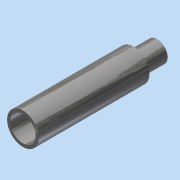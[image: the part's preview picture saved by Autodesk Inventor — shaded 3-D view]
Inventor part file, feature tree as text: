
AUTODESK INVENTOR PART (.ipt)
format: ipt  version: 2015 (Build 190159000, 159)  size: 100,352 bytes
history: native  units: in
note: dims shown in document units (in); Inventor stores cm internally (conversion verified against a paired STEP export)
features: extrude x3, sketch x3
ambient origin geometry x8: Origin, YZ Plane, XZ Plane, XY Plane, X Axis, Y Axis, Z Axis, Center Point
bodies: Solid1 (feature_tree)
feature tree (6):
  extrude  "Extrusion1"  Depth=0.5906in
  extrude  "Extrusion2"  Depth=2.0655in
  extrude  "Extrusion3"  Depth=0.4375in TaperAngle=0.0deg
  sketch  "Sketch1"  dims[d0=0.4724in d1=0.5906in]
  sketch  "Sketch2"  dims[d2=2.0655in d3=0.0in d4=0.3228in]
  sketch  "Sketch3"  dims[d5=0.3937in d6=0.4375in d7=0.0in d8=0.125in d9=0.0in]
